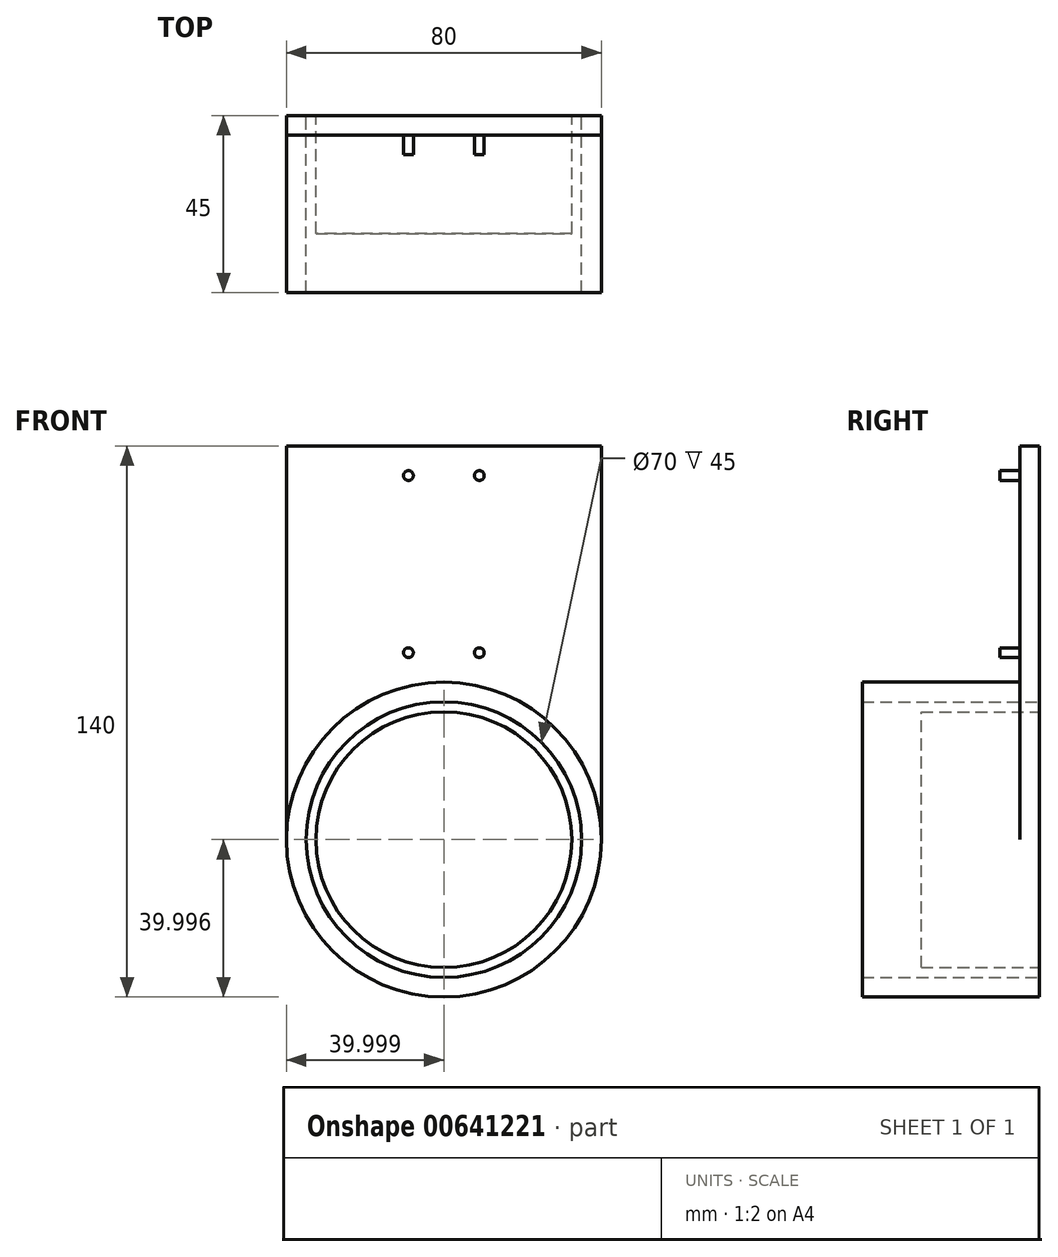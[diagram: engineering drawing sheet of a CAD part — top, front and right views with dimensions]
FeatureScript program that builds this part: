
annotation { "Feature Type Name" : "Feature", "Feature Type Description" : "" }
export const myFeature = defineFeature(function(context is Context, id is Id, definition is map)
    precondition{}
    {
        {
            var Q0;
            Q0=qCreatedBy(makeId("Front.planeOp"),FACE);
            var sketch = newSketch(context, id + "F0", { "sketchPlane" : qUnion([Q0])});
            skLineSegment(sketch, "E0.bottom", {"start": v(-79.2, 94.6) * mm, "end": v(0.8, 94.6) * mm});
            skLineSegment(sketch, "E0.top", {"start": v(-79.2, -5.4) * mm, "end": v(0.8, -5.4) * mm});
            skLineSegment(sketch, "E0.left", {"start": v(-79.2, 94.6) * mm, "end": v(-79.2, -5.4) * mm});
            skLineSegment(sketch, "E0.right", {"start": v(0.8, 94.6) * mm, "end": v(0.8, -5.4) * mm});
            skLineSegment(sketch, "E1.bottom", {"start": v(-79.2, 94.6) * mm, "end": v(-79.2, 94.6) * mm});
            skLineSegment(sketch, "E1.top", {"start": v(-79.2, -5.4) * mm, "end": v(-79.2, -5.4) * mm});
            skArc(sketch, "E2", {"start": v(-79.2, -5.4) * mm, "mid": v(-39.2, -45.4) * mm, "end": v(0.8, -5.4) * mm});
            skCircle(sketch, "E3", {"center": v(-39.2, -5.4) * mm, "radius": 40 * mm});
            skCircle(sketch, "E4", {"center": v(-48.2, 87.1) * mm, "radius": 1.25 * mm});
            skCircle(sketch, "E5", {"center": v(-30.2, 87.1) * mm, "radius": 1.25 * mm});
            skCircle(sketch, "E6", {"center": v(-30.2, 42.1) * mm, "radius": 1.25 * mm});
            skCircle(sketch, "E7", {"center": v(-48.2, 42.1) * mm, "radius": 1.25 * mm});
            skCircle(sketch, "E8", {"center": v(-39.2, -5.4) * mm, "radius": 35 * mm});
            skCircle(sketch, "E9", {"center": v(-39.2, -5.4) * mm, "radius": 32.5 * mm});
            skLineSegment(sketch, "E10.top", {"start": v(-35.95, 34.76) * mm, "end": v(-42.45, 34.76) * mm});
            skPoint(sketch, "E10.middle", {"position": v(-39.2, 28.5) * mm});
            skSolve(sketch);
        }
        {
            var Q0;
            Q0=makeQuery(id+"F0.imprint","IMPRINT",FACE,{"disambiguationData":[TD([[makeQuery(id+"F0.imprint","IMPRINT",EDGE,{"derivedFrom":sQuery(id+"F0.wireOp",EDGE,"E0.bottom")}),-1.0]])]});
            extrude(context, id + "F1", {"entities" : qUnion([Q0]), "depth" : 5 * mm, "offsetDistance" : 25 * mm});
        }
        {
            var Q0;
            {var subQ1=sQuery(id+"F0.wireOp",EDGE,"E0.top");var subQ3=sQuery(id+"F0.wireOp",EDGE,"E8");var subQ4=makeQuery(id+"F0.imprint","INTERSECT",VERTEX,{"disambiguationData":[OD(0.0)],"derivedFrom":[subQ1,subQ3]});Q0=makeQuery(id+"F0.imprint","IMPRINT",FACE,{"disambiguationData":[TD([[makeQuery(id+"F0.imprint","IMPRINT",EDGE,{"disambiguationData":[TD([[subQ4,-1.0]])],"derivedFrom":subQ3}),-1.0]])]});}
            var Q1;
            {var subQ1=sQuery(id+"F0.wireOp",EDGE,"E0.top");var subQ3=sQuery(id+"F0.wireOp",EDGE,"E8");var subQ4=makeQuery(id+"F0.imprint","INTERSECT",VERTEX,{"disambiguationData":[OD(0.0)],"derivedFrom":[subQ1,subQ3]});Q1=makeQuery(id+"F0.imprint","IMPRINT",FACE,{"disambiguationData":[TD([[makeQuery(id+"F0.imprint","IMPRINT",EDGE,{"disambiguationData":[TD([[subQ4,1.0]])],"derivedFrom":subQ3}),-1.0]])]});}
            extrude(context, id + "F2", {"entities" : qUnion([Q0, Q1]), "operationType" : NewBodyOperationType.ADD, "depth" : 45 * mm, "offsetDistance" : 25 * mm});
        }
        {
            var Q0;
            {var subQ0=sQuery(id+"F0.wireOp",EDGE,"E8");var subQ1=sQuery(id+"F0.wireOp",EDGE,"E0.top");var subQ2=makeQuery(id+"F0.imprint","INTERSECT",VERTEX,{"disambiguationData":[OD(0.0)],"derivedFrom":[subQ1,subQ0]});Q0=makeQuery(id+"F0.imprint","IMPRINT",FACE,{"disambiguationData":[TD([[makeQuery(id+"F0.imprint","IMPRINT",EDGE,{"disambiguationData":[TD([[subQ2,-1.0]])],"derivedFrom":subQ1}),1.0]])]});}
            var Q1;
            {var subQ0=sQuery(id+"F0.wireOp",EDGE,"E8");var subQ1=sQuery(id+"F0.wireOp",EDGE,"E0.top");var subQ2=makeQuery(id+"F0.imprint","INTERSECT",VERTEX,{"disambiguationData":[OD(0.0)],"derivedFrom":[subQ1,subQ0]});Q1=makeQuery(id+"F0.imprint","IMPRINT",FACE,{"disambiguationData":[TD([[makeQuery(id+"F0.imprint","IMPRINT",EDGE,{"disambiguationData":[TD([[subQ2,-1.0]])],"derivedFrom":subQ1}),-1.0]])]});}
            extrude(context, id + "F3", {"entities" : qUnion([Q0, Q1]), "operationType" : NewBodyOperationType.ADD, "depth" : 35 * mm, "offsetDistance" : 25 * mm});
        }
        {
            var Q0;
            {var subQ0=sQuery(id+"F0.wireOp",EDGE,"E9");var subQ1=sQuery(id+"F0.wireOp",EDGE,"E0.top");var subQ2=makeQuery(id+"F0.imprint","INTERSECT",VERTEX,{"disambiguationData":[OD(0.0)],"derivedFrom":[subQ1,subQ0]});Q0=makeQuery(id+"F0.imprint","IMPRINT",FACE,{"disambiguationData":[TD([[makeQuery(id+"F0.imprint","IMPRINT",EDGE,{"disambiguationData":[TD([[subQ2,-1.0]])],"derivedFrom":subQ1}),1.0]])]});}
            var Q1;
            {var subQ0=sQuery(id+"F0.wireOp",EDGE,"E9");var subQ1=sQuery(id+"F0.wireOp",EDGE,"E0.top");var subQ2=makeQuery(id+"F0.imprint","INTERSECT",VERTEX,{"disambiguationData":[OD(0.0)],"derivedFrom":[subQ1,subQ0]});Q1=makeQuery(id+"F0.imprint","IMPRINT",FACE,{"disambiguationData":[TD([[makeQuery(id+"F0.imprint","IMPRINT",EDGE,{"disambiguationData":[TD([[subQ2,-1.0]])],"derivedFrom":subQ1}),-1.0]])]});}
            extrude(context, id + "F4", {"entities" : qUnion([Q0, Q1]), "operationType" : NewBodyOperationType.ADD, "depth" : 30 * mm, "offsetDistance" : 25 * mm});
        }
        {
            var Q0;
            Q0=makeQuery(id+"F0.imprint","IMPRINT",FACE,{"disambiguationData":[TD([[makeQuery(id+"F0.imprint","IMPRINT",EDGE,{"derivedFrom":sQuery(id+"F0.wireOp",EDGE,"E6")}),1.0]])]});
            var Q1;
            Q1=makeQuery(id+"F0.imprint","IMPRINT",FACE,{"disambiguationData":[TD([[makeQuery(id+"F0.imprint","IMPRINT",EDGE,{"derivedFrom":sQuery(id+"F0.wireOp",EDGE,"E7")}),1.0]])]});
            var Q2;
            Q2=makeQuery(id+"F0.imprint","IMPRINT",FACE,{"disambiguationData":[TD([[makeQuery(id+"F0.imprint","IMPRINT",EDGE,{"derivedFrom":sQuery(id+"F0.wireOp",EDGE,"E4")}),1.0]])]});
            var Q3;
            Q3=makeQuery(id+"F0.imprint","IMPRINT",FACE,{"disambiguationData":[TD([[makeQuery(id+"F0.imprint","IMPRINT",EDGE,{"derivedFrom":sQuery(id+"F0.wireOp",EDGE,"E5")}),1.0]])]});
            extrude(context, id + "F5", {"entities" : qUnion([Q0, Q1, Q2, Q3]), "operationType" : NewBodyOperationType.ADD, "depth" : 10 * mm, "offsetDistance" : 25 * mm});
        }
    });
